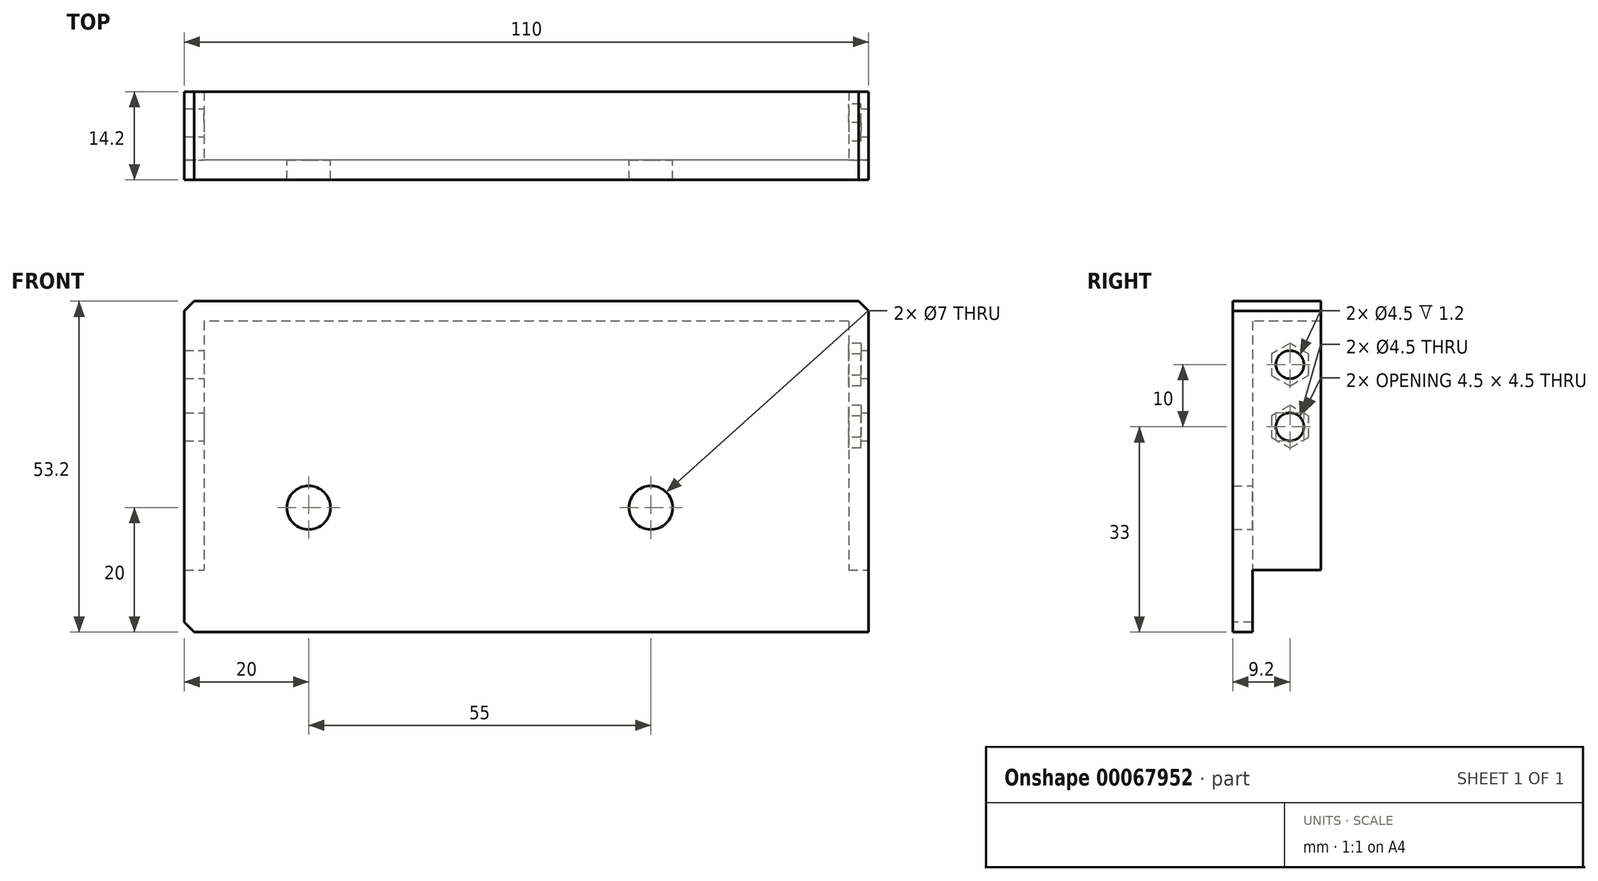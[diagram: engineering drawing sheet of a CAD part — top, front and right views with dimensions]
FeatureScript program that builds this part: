
annotation { "Feature Type Name" : "Feature", "Feature Type Description" : "" }
export const myFeature = defineFeature(function(context is Context, id is Id, definition is map)
    precondition{}
    {
        {
            var Q0;
            Q0=qCreatedBy(makeId("Front.planeOp"),FACE);
            var sketch = newSketch(context, id + "F0", { "sketchPlane" : qUnion([Q0])});
            skLineSegment(sketch, "E0.rect.bottom", {"start": v(55, 25) * mm, "end": v(-55, 25) * mm});
            skLineSegment(sketch, "E0.rect.top", {"start": v(55, -25) * mm, "end": v(-55, -25) * mm});
            skLineSegment(sketch, "E0.rect.left", {"start": v(55, 25) * mm, "end": v(55, -25) * mm});
            skLineSegment(sketch, "E0.rect.right", {"start": v(-55, 25) * mm, "end": v(-55, -25) * mm});
            skPoint(sketch, "E0.rect.middle", {"position": v(0, 0) * mm});
            skCircle(sketch, "E1", {"center": v(-35, -5) * mm, "radius": 3.5 * mm});
            skCircle(sketch, "E2", {"center": v(20, -5) * mm, "radius": 3.5 * mm});
            skSolve(sketch);
        }
        {
            var Q0;
            Q0 = qSketchRegion(id + "F0", true);
            extrude(context, id + "F1", {"entities" : qUnion([Q0]), "depth" : 3.2 * mm});
        }
        {
            var Q0;
            Q0=makeQuery(id+"F1.opExtrude","CAP_FACE",FACE,{"disambiguationData":[OSD([sQuery(id+"F0.wireOp",EDGE,"E0.rect.bottom"),sQuery(id+"F0.wireOp",EDGE,"E0.rect.top"),sQuery(id+"F0.wireOp",EDGE,"E0.rect.left"),sQuery(id+"F0.wireOp",EDGE,"E0.rect.right"),sQuery(id+"F0.wireOp",EDGE,"E1"),sQuery(id+"F0.wireOp",EDGE,"E2")])],"isStart":false});
            var sketch = newSketch(context, id + "F2", { "sketchPlane" : qUnion([Q0])});
            skLineSegment(sketch, "E3.rect.bottom", {"start": v(55, 25) * mm, "end": v(51.8, 25) * mm});
            skLineSegment(sketch, "E3.rect.left", {"start": v(55, 25) * mm, "end": v(55, -15) * mm});
            skLineSegment(sketch, "E3.rect.right", {"start": v(51.8, 25) * mm, "end": v(51.8, -15) * mm});
            skPoint(sketch, "E3.rect.middle", {"position": v(53.4, 0) * mm});
            skLineSegment(sketch, "E4.rect.bottom", {"start": v(-55, 25) * mm, "end": v(-51.8, 25) * mm});
            skLineSegment(sketch, "E4.rect.left", {"start": v(-55, 25) * mm, "end": v(-55, -15) * mm});
            skLineSegment(sketch, "E4.rect.right", {"start": v(-51.8, 25) * mm, "end": v(-51.8, -15) * mm});
            skPoint(sketch, "E4.rect.middle", {"position": v(-53.4, 0) * mm});
            skLineSegment(sketch, "E5", {"start": v(-55, -15) * mm, "end": v(-51.8, -15) * mm});
            skPoint(sketch, "E4.rect.top.end.orphan", {"position": v(-51.8, -25) * mm});
            skPoint(sketch, "E4.rect.top.start.orphan", {"position": v(-55, -25) * mm});
            skLineSegment(sketch, "E6", {"start": v(51.8, -15) * mm, "end": v(55, -15) * mm});
            skPoint(sketch, "E7.orphan", {"position": v(55, -25) * mm});
            skPoint(sketch, "E8.orphan", {"position": v(51.8, -25) * mm});
            skSolve(sketch);
        }
        {
            var Q0;
            Q0 = qSketchRegion(id + "F2", true);
            extrude(context, id + "F3", {"entities" : qUnion([Q0]), "operationType" : NewBodyOperationType.ADD, "oppositeDirection" : true, "depth" : 14.2 * mm});
        }
        {
            var Q0;
            Q0=makeQuery(id+"F3.boolean.opBoolean","MERGE",FACE,{"derivedFrom":[makeQuery(id+"F1.opExtrude","SWEPT_FACE",FACE,{"disambiguationData":[OSD([sQuery(id+"F0.wireOp",EDGE,"E0.rect.left")])]}),makeQuery(id+"F3.opExtrude","SWEPT_FACE",FACE,{"disambiguationData":[OSD([sQuery(id+"F2.wireOp",EDGE,"E3.rect.left")])]})]});
            var sketch = newSketch(context, id + "F4", { "sketchPlane" : qUnion([Q0])});
            skCircle(sketch, "E9", {"center": v(6, 18) * mm, "radius": 2.25 * mm});
            skCircle(sketch, "E10", {"center": v(6, 8) * mm, "radius": 2.25 * mm});
            skSolve(sketch);
        }
        {
            var Q0;
            Q0 = qSketchRegion(id + "F4", true);
            extrude(context, id + "F5", {"entities" : qUnion([Q0]), "operationType" : NewBodyOperationType.REMOVE, "endBound" : BoundingType.THROUGH_ALL, "oppositeDirection" : true, "depth" : 3.2 * mm});
        }
        {
            var Q0;
            Q0=makeQuery(id+"F1.opExtrude","CAP_FACE",FACE,{"disambiguationData":[OSD([sQuery(id+"F0.wireOp",EDGE,"E0.rect.bottom"),sQuery(id+"F0.wireOp",EDGE,"E0.rect.top"),sQuery(id+"F0.wireOp",EDGE,"E0.rect.left"),sQuery(id+"F0.wireOp",EDGE,"E0.rect.right"),sQuery(id+"F0.wireOp",EDGE,"E1"),sQuery(id+"F0.wireOp",EDGE,"E2")])],"isStart":false});
            var sketch = newSketch(context, id + "F6", { "sketchPlane" : qUnion([Q0])});
            skLineSegment(sketch, "E11.rect.bottom", {"start": v(55, 25) * mm, "end": v(-55, 25) * mm});
            skLineSegment(sketch, "E11.rect.top", {"start": v(55, 28.2) * mm, "end": v(-55, 28.2) * mm});
            skLineSegment(sketch, "E11.rect.left", {"start": v(55, 25) * mm, "end": v(55, 28.2) * mm});
            skLineSegment(sketch, "E11.rect.right", {"start": v(-55, 25) * mm, "end": v(-55, 28.2) * mm});
            skPoint(sketch, "E11.rect.middle", {"position": v(0, 26.6) * mm});
            skSolve(sketch);
        }
        {
            var Q0;
            Q0 = qSketchRegion(id + "F6", true);
            extrude(context, id + "F7", {"entities" : qUnion([Q0]), "operationType" : NewBodyOperationType.ADD, "oppositeDirection" : true, "depth" : 14.2 * mm});
        }
        {
            var Q0;
            Q0=makeQuery(id+"F7.opExtrude","SWEPT_EDGE",EDGE,{"disambiguationData":[OSD([sQuery(id+"F6.wireOp",EDGE,"E11.rect.top"),sQuery(id+"F6.wireOp",EDGE,"E11.rect.left")])]});
            var Q1;
            Q1=makeQuery(id+"F3.boolean.opBoolean","MERGE",EDGE,{"derivedFrom":[makeQuery(id+"F1.opExtrude","SWEPT_EDGE",EDGE,{"disambiguationData":[OSD([sQuery(id+"F0.wireOp",EDGE,"E0.rect.top"),sQuery(id+"F0.wireOp",EDGE,"E0.rect.left")])]}),makeQuery(id+"F3.opExtrude","SWEPT_EDGE",EDGE,{"disambiguationData":[OSD([sQuery(id+"F2.wireOp",EDGE,"E3.rect.top"),sQuery(id+"F2.wireOp",EDGE,"E3.rect.left")])]})]});
            var Q2;
            Q2=makeQuery(id+"F7.opExtrude","SWEPT_EDGE",EDGE,{"disambiguationData":[OSD([sQuery(id+"F6.wireOp",EDGE,"E11.rect.top"),sQuery(id+"F6.wireOp",EDGE,"E11.rect.right")])]});
            var Q3;
            Q3=makeQuery(id+"F1.opExtrude","SWEPT_EDGE",EDGE,{"disambiguationData":[OSD([sQuery(id+"F0.wireOp",EDGE,"E0.rect.top"),sQuery(id+"F0.wireOp",EDGE,"E0.rect.right")])]});
            chamfer(context, id + "F8", {"entities" : qUnion([Q0, Q1, Q2, Q3]), "width" : 1.6 * mm, "tangentPropagation" : true});
        }
        {
            var Q0;
            Q0=makeQuery(id+"F3.opExtrude","SWEPT_FACE",FACE,{"disambiguationData":[OSD([sQuery(id+"F2.wireOp",EDGE,"E3.rect.right")])]});
            var sketch = newSketch(context, id + "F9", { "sketchPlane" : qUnion([Q0])});
            skCircle(sketch, "E12.cCircle", {"center": v(-6, 8) * mm, "radius": 2.98 * mm, "construction": true});
            skLineSegment(sketch, "E12.0", {"start": v(-8.97, 6.28) * mm, "end": v(-8.97, 9.72) * mm});
            skLineSegment(sketch, "E12.1", {"start": v(-8.97, 9.72) * mm, "end": v(-6, 11.44) * mm});
            skLineSegment(sketch, "E12.2", {"start": v(-6, 11.44) * mm, "end": v(-3.03, 9.72) * mm});
            skLineSegment(sketch, "E12.3", {"start": v(-3.02, 9.72) * mm, "end": v(-3.02, 6.28) * mm});
            skLineSegment(sketch, "E12.4", {"start": v(-3.02, 6.28) * mm, "end": v(-6, 4.56) * mm});
            skLineSegment(sketch, "E12.5", {"start": v(-6, 4.56) * mm, "end": v(-8.97, 6.28) * mm});
            skPoint(sketch, "E12.0.midPoint", {"position": v(-8.97, 8) * mm});
            skCircle(sketch, "E13.cCircle", {"center": v(-6, 18) * mm, "radius": 2.98 * mm, "construction": true});
            skLineSegment(sketch, "E13.0", {"start": v(-8.97, 16.28) * mm, "end": v(-8.97, 19.72) * mm});
            skLineSegment(sketch, "E13.1", {"start": v(-8.97, 19.72) * mm, "end": v(-6, 21.44) * mm});
            skLineSegment(sketch, "E13.2", {"start": v(-6, 21.44) * mm, "end": v(-3.02, 19.72) * mm});
            skLineSegment(sketch, "E13.3", {"start": v(-3.02, 19.72) * mm, "end": v(-3.02, 16.28) * mm});
            skLineSegment(sketch, "E13.4", {"start": v(-3.02, 16.28) * mm, "end": v(-6, 14.56) * mm});
            skLineSegment(sketch, "E13.5", {"start": v(-6, 14.56) * mm, "end": v(-8.97, 16.28) * mm});
            skPoint(sketch, "E13.0.midPoint", {"position": v(-8.97, 18) * mm});
            skSolve(sketch);
        }
        {
            var Q0;
            Q0 = qSketchRegion(id + "F9", true);
            extrude(context, id + "F10", {"entities" : qUnion([Q0]), "operationType" : NewBodyOperationType.REMOVE, "oppositeDirection" : true, "depth" : 2 * mm});
        }
    });
